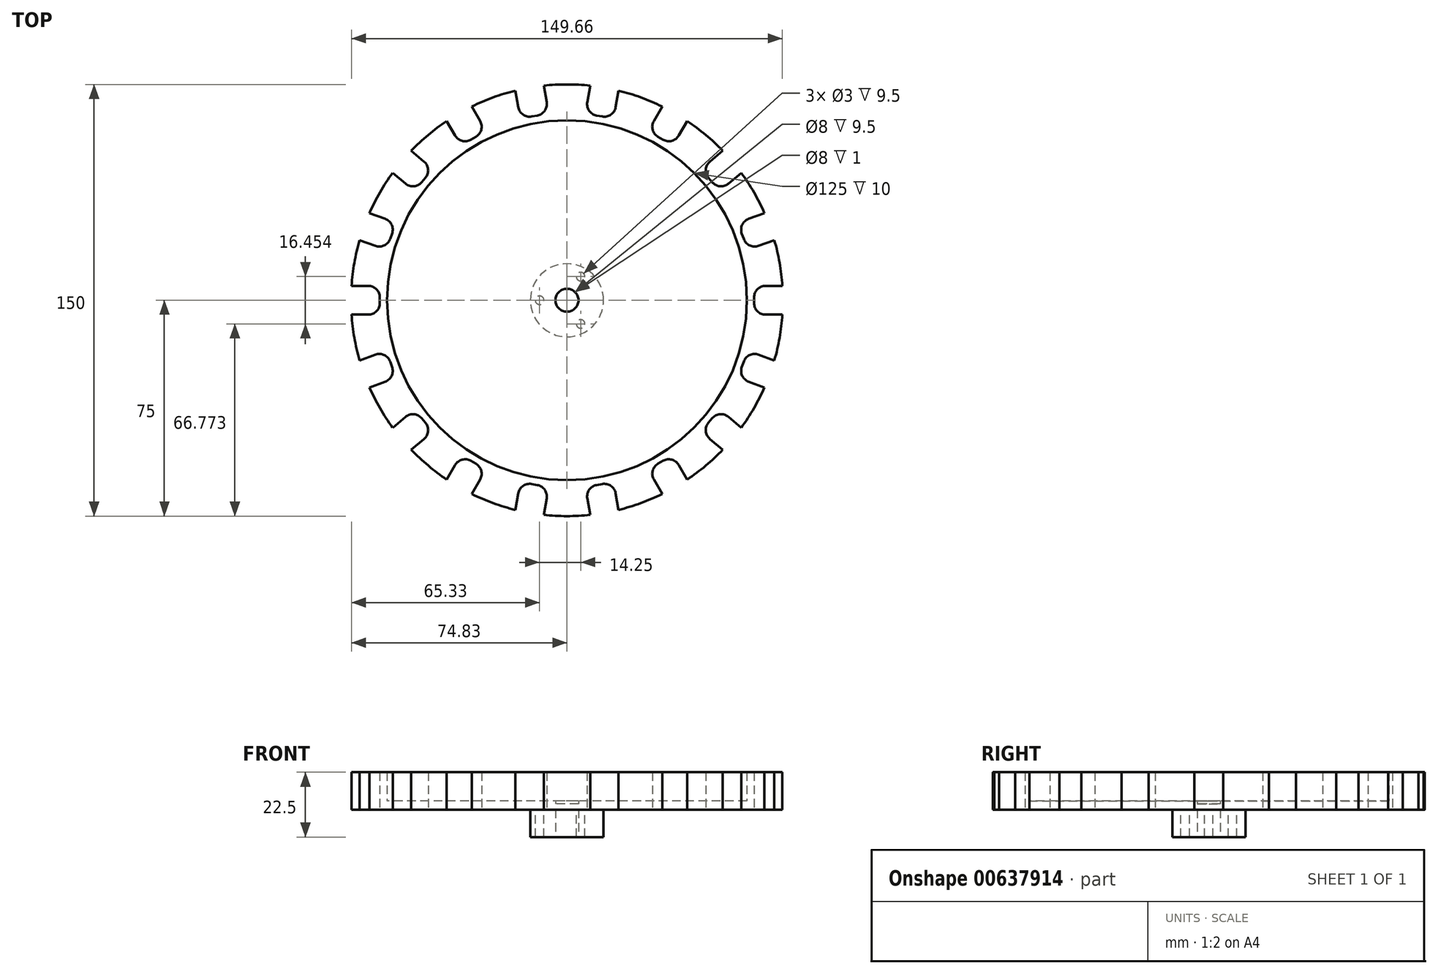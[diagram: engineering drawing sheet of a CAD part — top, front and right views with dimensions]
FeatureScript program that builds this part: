
annotation { "Feature Type Name" : "Feature", "Feature Type Description" : "" }
export const myFeature = defineFeature(function(context is Context, id is Id, definition is map)
    precondition{}
    {
        {
            var Q0;
            Q0=qCreatedBy(makeId("Top.planeOp"),FACE);
            var sketch = newSketch(context, id + "F0", { "sketchPlane" : qUnion([Q0])});
            skCircle(sketch, "E0", {"center": v(0, 0) * mm, "radius": 75 * mm});
            skCircle(sketch, "E1", {"center": v(0, 0) * mm, "radius": 62.5 * mm});
            skLineSegment(sketch, "E2", {"start": v(0, 0) * mm, "end": v(-124.02, 0) * mm, "construction": true});
            skPoint(sketch, "E3", {"position": v(-75, 0) * mm});
            skLineSegment(sketch, "E4.bottom", {"start": v(-75, -5) * mm, "end": v(-69, -5) * mm});
            skLineSegment(sketch, "E4.top", {"start": v(-75, 5) * mm, "end": v(-69, 5) * mm});
            skLineSegment(sketch, "E4.left", {"start": v(-75, -5) * mm, "end": v(-75, 5) * mm});
            skLineSegment(sketch, "E4.right", {"start": v(-65, -1) * mm, "end": v(-65, 1) * mm});
            skPoint(sketch, "E4.middle", {"position": v(-70, 0) * mm});
            skPoint(sketch, "E5.visualSharp", {"position": v(-65, 5) * mm});
            skArc(sketch, "E5.filletArc", {"start": v(-65, 1) * mm, "mid": v(-66.17, 3.83) * mm, "end": v(-69, 5) * mm});
            skPoint(sketch, "E6.visualSharp", {"position": v(-65, -5) * mm});
            skArc(sketch, "E6.filletArc", {"start": v(-69, -5) * mm, "mid": v(-66.17, -3.83) * mm, "end": v(-65, -1) * mm});
            skPoint(sketch, "E7.center", {"position": v(1.56, 0) * mm});
            skCircle(sketch, "E8", {"center": v(0, 0) * mm, "radius": 4 * mm});
            skCircle(sketch, "E9", {"center": v(0, 0) * mm, "radius": 12.7 * mm});
            skCircle(sketch, "E10", {"center": v(0, 0) * mm, "radius": 9.5 * mm, "construction": true});
            skCircle(sketch, "E11", {"center": v(-9.5, 0) * mm, "radius": 1.5 * mm});
            skCircle(sketch, "E12.1.0", {"center": v(-4.75, -8.23) * mm, "radius": 1.5 * mm});
            skCircle(sketch, "E12.2.0", {"center": v(4.75, -8.23) * mm, "radius": 1.5 * mm});
            skCircle(sketch, "E12.3.0", {"center": v(9.5, 0) * mm, "radius": 1.5 * mm});
            skCircle(sketch, "E12.4.0", {"center": v(4.75, 8.23) * mm, "radius": 1.5 * mm});
            skCircle(sketch, "E12.5.0", {"center": v(-4.75, 8.23) * mm, "radius": 1.5 * mm});
            skPoint(sketch, "E13.1.0", {"position": v(-62.8, -17.53) * mm});
            skPoint(sketch, "E13.1.1", {"position": v(-70.48, -25.65) * mm});
            skPoint(sketch, "E13.1.2", {"position": v(-59.37, -26.93) * mm});
            skPoint(sketch, "E13.1.3", {"position": v(-65.78, -23.94) * mm});
            skArc(sketch, "E13.1.4", {"start": v(-63.13, -28.3) * mm, "mid": v(-60.87, -26.23) * mm, "end": v(-60.74, -23.17) * mm});
            skArc(sketch, "E13.1.5", {"start": v(-61.42, -21.3) * mm, "mid": v(-63.5, -19.03) * mm, "end": v(-66.55, -18.9) * mm});
            skLineSegment(sketch, "E13.1.6", {"start": v(-68.77, -30.35) * mm, "end": v(-72.19, -20.95) * mm});
            skLineSegment(sketch, "E13.1.7", {"start": v(-60.74, -23.17) * mm, "end": v(-61.42, -21.3) * mm});
            skLineSegment(sketch, "E13.1.8", {"start": v(-72.19, -20.95) * mm, "end": v(-66.55, -18.9) * mm});
            skLineSegment(sketch, "E13.1.9", {"start": v(-68.77, -30.35) * mm, "end": v(-63.13, -28.3) * mm});
            skPoint(sketch, "E13.2.0", {"position": v(-53, -37.95) * mm});
            skPoint(sketch, "E13.2.1", {"position": v(-57.45, -48.2) * mm});
            skPoint(sketch, "E13.2.2", {"position": v(-46.58, -45.61) * mm});
            skPoint(sketch, "E13.2.3", {"position": v(-53.62, -45) * mm});
            skArc(sketch, "E13.2.4", {"start": v(-49.64, -48.18) * mm, "mid": v(-48.23, -45.47) * mm, "end": v(-49.15, -42.55) * mm});
            skArc(sketch, "E13.2.5", {"start": v(-50.44, -41.02) * mm, "mid": v(-53.15, -39.6) * mm, "end": v(-56.07, -40.52) * mm});
            skLineSegment(sketch, "E13.2.6", {"start": v(-54.24, -52.04) * mm, "end": v(-60.67, -44.38) * mm});
            skLineSegment(sketch, "E13.2.7", {"start": v(-49.15, -42.55) * mm, "end": v(-50.44, -41.02) * mm});
            skLineSegment(sketch, "E13.2.8", {"start": v(-60.67, -44.38) * mm, "end": v(-56.07, -40.52) * mm});
            skLineSegment(sketch, "E13.2.9", {"start": v(-54.24, -52.04) * mm, "end": v(-49.64, -48.18) * mm});
            skPoint(sketch, "E13.3.0", {"position": v(-36.83, -53.8) * mm});
            skPoint(sketch, "E13.3.1", {"position": v(-37.5, -64.95) * mm});
            skPoint(sketch, "E13.3.2", {"position": v(-28.17, -58.8) * mm});
            skPoint(sketch, "E13.3.3", {"position": v(-35, -60.62) * mm});
            skArc(sketch, "E13.3.4", {"start": v(-30.17, -62.26) * mm, "mid": v(-29.77, -59.22) * mm, "end": v(-31.63, -56.8) * mm});
            skArc(sketch, "E13.3.5", {"start": v(-33.37, -55.8) * mm, "mid": v(-36.4, -55.4) * mm, "end": v(-38.83, -57.26) * mm});
            skLineSegment(sketch, "E13.3.6", {"start": v(-33.17, -67.45) * mm, "end": v(-41.83, -62.45) * mm});
            skLineSegment(sketch, "E13.3.7", {"start": v(-31.63, -56.8) * mm, "end": v(-33.37, -55.8) * mm});
            skLineSegment(sketch, "E13.3.8", {"start": v(-41.83, -62.45) * mm, "end": v(-38.83, -57.26) * mm});
            skLineSegment(sketch, "E13.3.9", {"start": v(-33.17, -67.45) * mm, "end": v(-30.17, -62.26) * mm});
            skPoint(sketch, "E13.4.0", {"position": v(-16.21, -63.14) * mm});
            skPoint(sketch, "E13.4.1", {"position": v(-13.02, -73.86) * mm});
            skPoint(sketch, "E13.4.2", {"position": v(-6.36, -64.88) * mm});
            skPoint(sketch, "E13.4.3", {"position": v(-12.16, -68.94) * mm});
            skArc(sketch, "E13.4.4", {"start": v(-7.06, -68.82) * mm, "mid": v(-7.72, -65.83) * mm, "end": v(-10.3, -64.19) * mm});
            skArc(sketch, "E13.4.5", {"start": v(-12.27, -63.84) * mm, "mid": v(-15.26, -64.5) * mm, "end": v(-16.9, -67.08) * mm});
            skLineSegment(sketch, "E13.4.6", {"start": v(-8.1, -74.73) * mm, "end": v(-17.95, -73) * mm});
            skLineSegment(sketch, "E13.4.7", {"start": v(-10.3, -64.19) * mm, "end": v(-12.27, -63.84) * mm});
            skLineSegment(sketch, "E13.4.8", {"start": v(-17.95, -73) * mm, "end": v(-16.9, -67.08) * mm});
            skLineSegment(sketch, "E13.4.9", {"start": v(-8.1, -74.73) * mm, "end": v(-7.06, -68.82) * mm});
            skPoint(sketch, "E13.5.0", {"position": v(6.36, -64.88) * mm});
            skPoint(sketch, "E13.5.1", {"position": v(13.02, -73.86) * mm});
            skPoint(sketch, "E13.5.2", {"position": v(16.21, -63.14) * mm});
            skPoint(sketch, "E13.5.3", {"position": v(12.16, -68.94) * mm});
            skArc(sketch, "E13.5.4", {"start": v(16.9, -67.08) * mm, "mid": v(15.26, -64.5) * mm, "end": v(12.27, -63.84) * mm});
            skArc(sketch, "E13.5.5", {"start": v(10.3, -64.19) * mm, "mid": v(7.72, -65.83) * mm, "end": v(7.06, -68.82) * mm});
            skLineSegment(sketch, "E13.5.6", {"start": v(17.95, -73) * mm, "end": v(8.1, -74.73) * mm});
            skLineSegment(sketch, "E13.5.7", {"start": v(12.27, -63.84) * mm, "end": v(10.3, -64.19) * mm});
            skLineSegment(sketch, "E13.5.8", {"start": v(8.1, -74.73) * mm, "end": v(7.06, -68.82) * mm});
            skLineSegment(sketch, "E13.5.9", {"start": v(17.95, -73) * mm, "end": v(16.9, -67.08) * mm});
            skPoint(sketch, "E13.6.0", {"position": v(28.17, -58.8) * mm});
            skPoint(sketch, "E13.6.1", {"position": v(37.5, -64.95) * mm});
            skPoint(sketch, "E13.6.2", {"position": v(36.83, -53.8) * mm});
            skPoint(sketch, "E13.6.3", {"position": v(35, -60.62) * mm});
            skArc(sketch, "E13.6.4", {"start": v(38.83, -57.26) * mm, "mid": v(36.4, -55.4) * mm, "end": v(33.37, -55.8) * mm});
            skArc(sketch, "E13.6.5", {"start": v(31.63, -56.8) * mm, "mid": v(29.77, -59.22) * mm, "end": v(30.17, -62.26) * mm});
            skLineSegment(sketch, "E13.6.6", {"start": v(41.83, -62.45) * mm, "end": v(33.17, -67.45) * mm});
            skLineSegment(sketch, "E13.6.7", {"start": v(33.37, -55.8) * mm, "end": v(31.63, -56.8) * mm});
            skLineSegment(sketch, "E13.6.8", {"start": v(33.17, -67.45) * mm, "end": v(30.17, -62.26) * mm});
            skLineSegment(sketch, "E13.6.9", {"start": v(41.83, -62.45) * mm, "end": v(38.83, -57.26) * mm});
            skPoint(sketch, "E13.7.0", {"position": v(46.58, -45.61) * mm});
            skPoint(sketch, "E13.7.1", {"position": v(57.45, -48.2) * mm});
            skPoint(sketch, "E13.7.2", {"position": v(53, -37.95) * mm});
            skPoint(sketch, "E13.7.3", {"position": v(53.62, -45) * mm});
            skArc(sketch, "E13.7.4", {"start": v(56.07, -40.52) * mm, "mid": v(53.15, -39.6) * mm, "end": v(50.44, -41.02) * mm});
            skArc(sketch, "E13.7.5", {"start": v(49.15, -42.55) * mm, "mid": v(48.23, -45.47) * mm, "end": v(49.64, -48.18) * mm});
            skLineSegment(sketch, "E13.7.6", {"start": v(60.67, -44.38) * mm, "end": v(54.24, -52.04) * mm});
            skLineSegment(sketch, "E13.7.7", {"start": v(50.44, -41.02) * mm, "end": v(49.15, -42.55) * mm});
            skLineSegment(sketch, "E13.7.8", {"start": v(54.24, -52.04) * mm, "end": v(49.64, -48.18) * mm});
            skLineSegment(sketch, "E13.7.9", {"start": v(60.67, -44.38) * mm, "end": v(56.07, -40.52) * mm});
            skPoint(sketch, "E13.8.0", {"position": v(59.37, -26.93) * mm});
            skPoint(sketch, "E13.8.1", {"position": v(70.48, -25.65) * mm});
            skPoint(sketch, "E13.8.2", {"position": v(62.8, -17.53) * mm});
            skPoint(sketch, "E13.8.3", {"position": v(65.78, -23.94) * mm});
            skArc(sketch, "E13.8.4", {"start": v(66.55, -18.9) * mm, "mid": v(63.5, -19.03) * mm, "end": v(61.42, -21.3) * mm});
            skArc(sketch, "E13.8.5", {"start": v(60.74, -23.17) * mm, "mid": v(60.87, -26.23) * mm, "end": v(63.13, -28.3) * mm});
            skLineSegment(sketch, "E13.8.6", {"start": v(72.19, -20.95) * mm, "end": v(68.77, -30.35) * mm});
            skLineSegment(sketch, "E13.8.7", {"start": v(61.42, -21.3) * mm, "end": v(60.74, -23.17) * mm});
            skLineSegment(sketch, "E13.8.8", {"start": v(68.77, -30.35) * mm, "end": v(63.13, -28.3) * mm});
            skLineSegment(sketch, "E13.8.9", {"start": v(72.19, -20.95) * mm, "end": v(66.55, -18.9) * mm});
            skPoint(sketch, "E13.9.0", {"position": v(65, -5) * mm});
            skPoint(sketch, "E13.9.1", {"position": v(75, 0) * mm});
            skPoint(sketch, "E13.9.2", {"position": v(65, 5) * mm});
            skPoint(sketch, "E13.9.3", {"position": v(70, 0) * mm});
            skArc(sketch, "E13.9.4", {"start": v(69, 5) * mm, "mid": v(66.17, 3.83) * mm, "end": v(65, 1) * mm});
            skArc(sketch, "E13.9.5", {"start": v(65, -1) * mm, "mid": v(66.17, -3.83) * mm, "end": v(69, -5) * mm});
            skLineSegment(sketch, "E13.9.6", {"start": v(75, 5) * mm, "end": v(75, -5) * mm});
            skLineSegment(sketch, "E13.9.7", {"start": v(65, 1) * mm, "end": v(65, -1) * mm});
            skLineSegment(sketch, "E13.9.8", {"start": v(75, -5) * mm, "end": v(69, -5) * mm});
            skLineSegment(sketch, "E13.9.9", {"start": v(75, 5) * mm, "end": v(69, 5) * mm});
            skPoint(sketch, "E13.10.0", {"position": v(62.8, 17.53) * mm});
            skPoint(sketch, "E13.10.1", {"position": v(70.48, 25.65) * mm});
            skPoint(sketch, "E13.10.2", {"position": v(59.37, 26.93) * mm});
            skPoint(sketch, "E13.10.3", {"position": v(65.78, 23.94) * mm});
            skArc(sketch, "E13.10.4", {"start": v(63.13, 28.3) * mm, "mid": v(60.87, 26.23) * mm, "end": v(60.74, 23.17) * mm});
            skArc(sketch, "E13.10.5", {"start": v(61.42, 21.3) * mm, "mid": v(63.5, 19.03) * mm, "end": v(66.55, 18.9) * mm});
            skLineSegment(sketch, "E13.10.6", {"start": v(68.77, 30.35) * mm, "end": v(72.19, 20.95) * mm});
            skLineSegment(sketch, "E13.10.7", {"start": v(60.74, 23.17) * mm, "end": v(61.42, 21.3) * mm});
            skLineSegment(sketch, "E13.10.8", {"start": v(72.19, 20.95) * mm, "end": v(66.55, 18.9) * mm});
            skLineSegment(sketch, "E13.10.9", {"start": v(68.77, 30.35) * mm, "end": v(63.13, 28.3) * mm});
            skPoint(sketch, "E13.11.0", {"position": v(53, 37.95) * mm});
            skPoint(sketch, "E13.11.1", {"position": v(57.45, 48.2) * mm});
            skPoint(sketch, "E13.11.2", {"position": v(46.58, 45.61) * mm});
            skPoint(sketch, "E13.11.3", {"position": v(53.62, 45) * mm});
            skArc(sketch, "E13.11.4", {"start": v(49.64, 48.18) * mm, "mid": v(48.23, 45.47) * mm, "end": v(49.15, 42.55) * mm});
            skArc(sketch, "E13.11.5", {"start": v(50.44, 41.02) * mm, "mid": v(53.15, 39.6) * mm, "end": v(56.07, 40.52) * mm});
            skLineSegment(sketch, "E13.11.6", {"start": v(54.24, 52.04) * mm, "end": v(60.67, 44.38) * mm});
            skLineSegment(sketch, "E13.11.7", {"start": v(49.15, 42.55) * mm, "end": v(50.44, 41.02) * mm});
            skLineSegment(sketch, "E13.11.8", {"start": v(60.67, 44.38) * mm, "end": v(56.07, 40.52) * mm});
            skLineSegment(sketch, "E13.11.9", {"start": v(54.24, 52.04) * mm, "end": v(49.64, 48.18) * mm});
            skPoint(sketch, "E13.12.0", {"position": v(36.83, 53.8) * mm});
            skPoint(sketch, "E13.12.1", {"position": v(37.5, 64.95) * mm});
            skPoint(sketch, "E13.12.2", {"position": v(28.17, 58.8) * mm});
            skPoint(sketch, "E13.12.3", {"position": v(35, 60.62) * mm});
            skArc(sketch, "E13.12.4", {"start": v(30.17, 62.26) * mm, "mid": v(29.77, 59.22) * mm, "end": v(31.63, 56.8) * mm});
            skArc(sketch, "E13.12.5", {"start": v(33.37, 55.8) * mm, "mid": v(36.4, 55.4) * mm, "end": v(38.83, 57.26) * mm});
            skLineSegment(sketch, "E13.12.6", {"start": v(33.17, 67.45) * mm, "end": v(41.83, 62.45) * mm});
            skLineSegment(sketch, "E13.12.7", {"start": v(31.63, 56.8) * mm, "end": v(33.37, 55.8) * mm});
            skLineSegment(sketch, "E13.12.8", {"start": v(41.83, 62.45) * mm, "end": v(38.83, 57.26) * mm});
            skLineSegment(sketch, "E13.12.9", {"start": v(33.17, 67.45) * mm, "end": v(30.17, 62.26) * mm});
            skPoint(sketch, "E13.13.0", {"position": v(16.21, 63.14) * mm});
            skPoint(sketch, "E13.13.1", {"position": v(13.02, 73.86) * mm});
            skPoint(sketch, "E13.13.2", {"position": v(6.36, 64.88) * mm});
            skPoint(sketch, "E13.13.3", {"position": v(12.16, 68.94) * mm});
            skArc(sketch, "E13.13.4", {"start": v(7.06, 68.82) * mm, "mid": v(7.72, 65.83) * mm, "end": v(10.3, 64.19) * mm});
            skArc(sketch, "E13.13.5", {"start": v(12.27, 63.84) * mm, "mid": v(15.26, 64.5) * mm, "end": v(16.9, 67.08) * mm});
            skLineSegment(sketch, "E13.13.6", {"start": v(8.1, 74.73) * mm, "end": v(17.95, 73) * mm});
            skLineSegment(sketch, "E13.13.7", {"start": v(10.3, 64.19) * mm, "end": v(12.27, 63.84) * mm});
            skLineSegment(sketch, "E13.13.8", {"start": v(17.95, 73) * mm, "end": v(16.9, 67.08) * mm});
            skLineSegment(sketch, "E13.13.9", {"start": v(8.1, 74.73) * mm, "end": v(7.06, 68.82) * mm});
            skPoint(sketch, "E13.14.0", {"position": v(-6.36, 64.88) * mm});
            skPoint(sketch, "E13.14.1", {"position": v(-13.02, 73.86) * mm});
            skPoint(sketch, "E13.14.2", {"position": v(-16.21, 63.14) * mm});
            skPoint(sketch, "E13.14.3", {"position": v(-12.16, 68.94) * mm});
            skArc(sketch, "E13.14.4", {"start": v(-16.9, 67.08) * mm, "mid": v(-15.26, 64.5) * mm, "end": v(-12.27, 63.84) * mm});
            skArc(sketch, "E13.14.5", {"start": v(-10.3, 64.19) * mm, "mid": v(-7.72, 65.83) * mm, "end": v(-7.06, 68.82) * mm});
            skLineSegment(sketch, "E13.14.6", {"start": v(-17.95, 73) * mm, "end": v(-8.1, 74.73) * mm});
            skLineSegment(sketch, "E13.14.7", {"start": v(-12.27, 63.84) * mm, "end": v(-10.3, 64.19) * mm});
            skLineSegment(sketch, "E13.14.8", {"start": v(-8.1, 74.73) * mm, "end": v(-7.06, 68.82) * mm});
            skLineSegment(sketch, "E13.14.9", {"start": v(-17.95, 73) * mm, "end": v(-16.9, 67.08) * mm});
            skPoint(sketch, "E13.15.0", {"position": v(-28.17, 58.8) * mm});
            skPoint(sketch, "E13.15.1", {"position": v(-37.5, 64.95) * mm});
            skPoint(sketch, "E13.15.2", {"position": v(-36.83, 53.8) * mm});
            skPoint(sketch, "E13.15.3", {"position": v(-35, 60.62) * mm});
            skArc(sketch, "E13.15.4", {"start": v(-38.83, 57.26) * mm, "mid": v(-36.4, 55.4) * mm, "end": v(-33.37, 55.8) * mm});
            skArc(sketch, "E13.15.5", {"start": v(-31.63, 56.8) * mm, "mid": v(-29.77, 59.22) * mm, "end": v(-30.17, 62.26) * mm});
            skLineSegment(sketch, "E13.15.6", {"start": v(-41.83, 62.45) * mm, "end": v(-33.17, 67.45) * mm});
            skLineSegment(sketch, "E13.15.7", {"start": v(-33.37, 55.8) * mm, "end": v(-31.63, 56.8) * mm});
            skLineSegment(sketch, "E13.15.8", {"start": v(-33.17, 67.45) * mm, "end": v(-30.17, 62.26) * mm});
            skLineSegment(sketch, "E13.15.9", {"start": v(-41.83, 62.45) * mm, "end": v(-38.83, 57.26) * mm});
            skPoint(sketch, "E13.16.0", {"position": v(-46.58, 45.61) * mm});
            skPoint(sketch, "E13.16.1", {"position": v(-57.45, 48.2) * mm});
            skPoint(sketch, "E13.16.2", {"position": v(-53, 37.95) * mm});
            skPoint(sketch, "E13.16.3", {"position": v(-53.62, 45) * mm});
            skArc(sketch, "E13.16.4", {"start": v(-56.07, 40.52) * mm, "mid": v(-53.15, 39.6) * mm, "end": v(-50.44, 41.02) * mm});
            skArc(sketch, "E13.16.5", {"start": v(-49.15, 42.55) * mm, "mid": v(-48.23, 45.47) * mm, "end": v(-49.64, 48.18) * mm});
            skLineSegment(sketch, "E13.16.6", {"start": v(-60.67, 44.38) * mm, "end": v(-54.24, 52.04) * mm});
            skLineSegment(sketch, "E13.16.7", {"start": v(-50.44, 41.02) * mm, "end": v(-49.15, 42.55) * mm});
            skLineSegment(sketch, "E13.16.8", {"start": v(-54.24, 52.04) * mm, "end": v(-49.64, 48.18) * mm});
            skLineSegment(sketch, "E13.16.9", {"start": v(-60.67, 44.38) * mm, "end": v(-56.07, 40.52) * mm});
            skPoint(sketch, "E13.17.0", {"position": v(-59.37, 26.93) * mm});
            skPoint(sketch, "E13.17.1", {"position": v(-70.48, 25.65) * mm});
            skPoint(sketch, "E13.17.2", {"position": v(-62.8, 17.53) * mm});
            skPoint(sketch, "E13.17.3", {"position": v(-65.78, 23.94) * mm});
            skArc(sketch, "E13.17.4", {"start": v(-66.55, 18.9) * mm, "mid": v(-63.5, 19.03) * mm, "end": v(-61.42, 21.3) * mm});
            skArc(sketch, "E13.17.5", {"start": v(-60.74, 23.17) * mm, "mid": v(-60.87, 26.23) * mm, "end": v(-63.13, 28.3) * mm});
            skLineSegment(sketch, "E13.17.6", {"start": v(-72.19, 20.95) * mm, "end": v(-68.77, 30.35) * mm});
            skLineSegment(sketch, "E13.17.7", {"start": v(-61.42, 21.3) * mm, "end": v(-60.74, 23.17) * mm});
            skLineSegment(sketch, "E13.17.8", {"start": v(-68.77, 30.35) * mm, "end": v(-63.13, 28.3) * mm});
            skLineSegment(sketch, "E13.17.9", {"start": v(-72.19, 20.95) * mm, "end": v(-66.55, 18.9) * mm});
            skSolve(sketch);
        }
        {
            var Q0;
            Q0=makeQuery(id+"F0.imprint","IMPRINT",FACE,{"disambiguationData":[TD([[makeQuery(id+"F0.imprint","IMPRINT",EDGE,{"derivedFrom":sQuery(id+"F0.wireOp",EDGE,"E1")}),1.0]])]});
            var Q1;
            Q1=makeQuery(id+"F0.imprint","IMPRINT",FACE,{"disambiguationData":[TD([[makeQuery(id+"F0.imprint","IMPRINT",EDGE,{"derivedFrom":sQuery(id+"F0.wireOp",EDGE,"E8")}),-1.0]])]});
            var Q2;
            Q2=makeQuery(id+"F0.imprint","IMPRINT",FACE,{"disambiguationData":[TD([[makeQuery(id+"F0.imprint","IMPRINT",EDGE,{"derivedFrom":sQuery(id+"F0.wireOp",EDGE,"E12.3.0")}),1.0]])]});
            var Q3;
            Q3=makeQuery(id+"F0.imprint","IMPRINT",FACE,{"disambiguationData":[TD([[makeQuery(id+"F0.imprint","IMPRINT",EDGE,{"derivedFrom":sQuery(id+"F0.wireOp",EDGE,"E12.4.0")}),1.0]])]});
            var Q4;
            Q4=makeQuery(id+"F0.imprint","IMPRINT",FACE,{"disambiguationData":[TD([[makeQuery(id+"F0.imprint","IMPRINT",EDGE,{"derivedFrom":sQuery(id+"F0.wireOp",EDGE,"E12.5.0")}),1.0]])]});
            var Q5;
            Q5=makeQuery(id+"F0.imprint","IMPRINT",FACE,{"disambiguationData":[TD([[makeQuery(id+"F0.imprint","IMPRINT",EDGE,{"derivedFrom":sQuery(id+"F0.wireOp",EDGE,"E11")}),1.0]])]});
            var Q6;
            Q6=makeQuery(id+"F0.imprint","IMPRINT",FACE,{"disambiguationData":[TD([[makeQuery(id+"F0.imprint","IMPRINT",EDGE,{"derivedFrom":sQuery(id+"F0.wireOp",EDGE,"E12.1.0")}),1.0]])]});
            var Q7;
            Q7=makeQuery(id+"F0.imprint","IMPRINT",FACE,{"disambiguationData":[TD([[makeQuery(id+"F0.imprint","IMPRINT",EDGE,{"derivedFrom":sQuery(id+"F0.wireOp",EDGE,"E12.2.0")}),1.0]])]});
            extrude(context, id + "F1", {"entities" : qUnion([Q0, Q1, Q2, Q3, Q4, Q5, Q6, Q7]), "depth" : 3 * mm, "offsetDistance" : 25 * mm});
        }
        {
            var Q0;
            Q0=makeQuery(id+"F0.imprint","IMPRINT",FACE,{"disambiguationData":[TD([[makeQuery(id+"F0.imprint","IMPRINT",EDGE,{"derivedFrom":sQuery(id+"F0.wireOp",EDGE,"E1")}),-1.0]])]});
            extrude(context, id + "F2", {"entities" : qUnion([Q0]), "operationType" : NewBodyOperationType.ADD, "depth" : 13 * mm, "offsetDistance" : 25 * mm});
        }
        {
            var Q0;
            Q0=makeQuery(id+"F0.imprint","IMPRINT",FACE,{"disambiguationData":[TD([[makeQuery(id+"F0.imprint","IMPRINT",EDGE,{"derivedFrom":sQuery(id+"F0.wireOp",EDGE,"E8")}),-1.0]])]});
            var Q1;
            Q1=makeQuery(id+"F0.imprint","IMPRINT",FACE,{"disambiguationData":[TD([[makeQuery(id+"F0.imprint","IMPRINT",EDGE,{"derivedFrom":sQuery(id+"F0.wireOp",EDGE,"E12.5.0")}),1.0]])]});
            var Q2;
            Q2=makeQuery(id+"F0.imprint","IMPRINT",FACE,{"disambiguationData":[TD([[makeQuery(id+"F0.imprint","IMPRINT",EDGE,{"derivedFrom":sQuery(id+"F0.wireOp",EDGE,"E12.3.0")}),1.0]])]});
            var Q3;
            Q3=makeQuery(id+"F0.imprint","IMPRINT",FACE,{"disambiguationData":[TD([[makeQuery(id+"F0.imprint","IMPRINT",EDGE,{"derivedFrom":sQuery(id+"F0.wireOp",EDGE,"E12.1.0")}),1.0]])]});
            extrude(context, id + "F3", {"entities" : qUnion([Q0, Q1, Q2, Q3]), "operationType" : NewBodyOperationType.ADD, "oppositeDirection" : true, "depth" : 9.5 * mm, "offsetDistance" : 25 * mm});
        }
        {
            var Q0;
            Q0=makeQuery(id+"F0.imprint","IMPRINT",FACE,{"disambiguationData":[TD([[makeQuery(id+"F0.imprint","IMPRINT",EDGE,{"derivedFrom":sQuery(id+"F0.wireOp",EDGE,"E8")}),1.0]])]});
            extrude(context, id + "F4", {"entities" : qUnion([Q0]), "operationType" : NewBodyOperationType.ADD, "depth" : 2 * mm, "offsetDistance" : 25 * mm});
        }
    });
